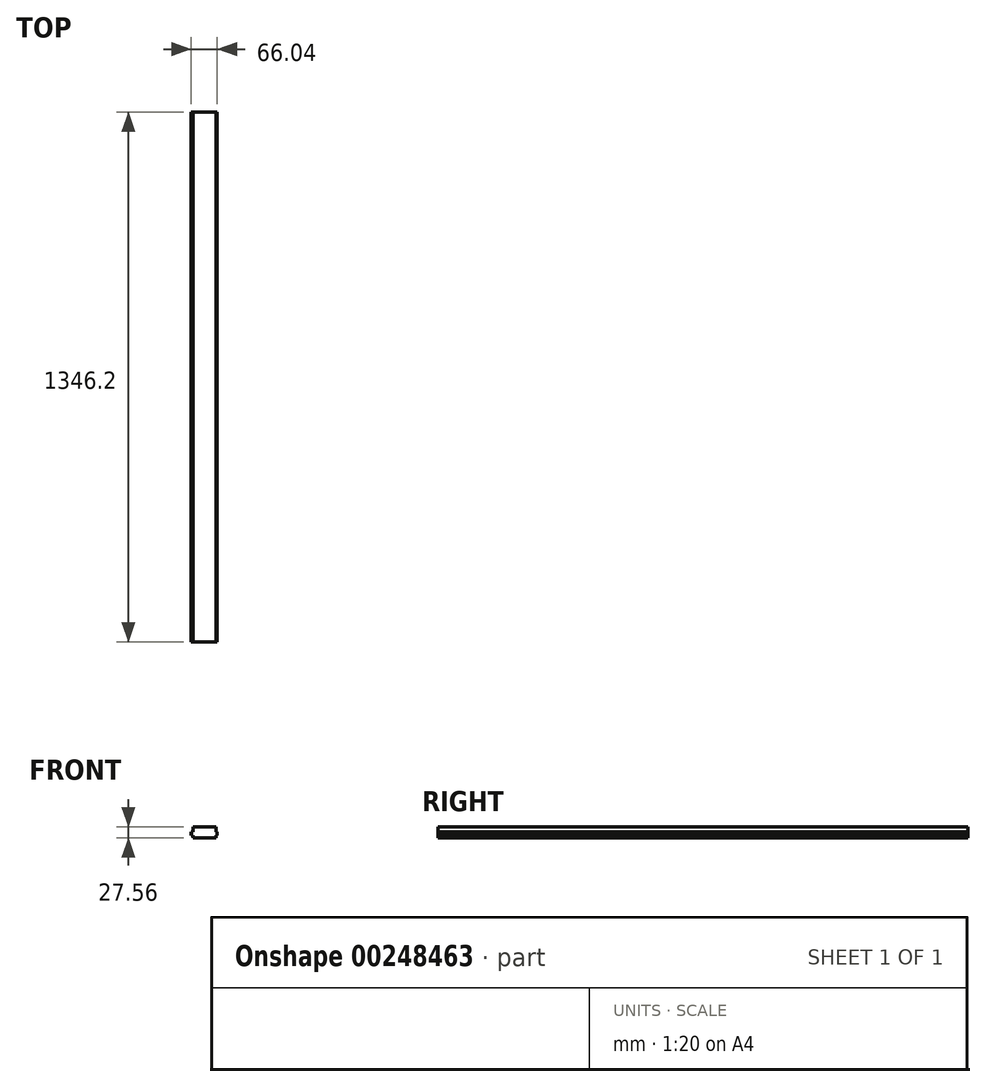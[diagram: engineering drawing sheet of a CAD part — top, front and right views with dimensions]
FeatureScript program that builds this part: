
annotation { "Feature Type Name" : "Feature", "Feature Type Description" : "" }
export const myFeature = defineFeature(function(context is Context, id is Id, definition is map)
    precondition{}
    {
        {
            var Q0;
            Q0=qCreatedBy(makeId("Front.planeOp"),FACE);
            var sketch = newSketch(context, id + "F0", { "sketchPlane" : qUnion([Q0])});
            skLineSegment(sketch, "E0", {"start": v(0, 0) * mm, "end": v(0, 73.02) * mm, "construction": true});
            skLineSegment(sketch, "E1", {"start": v(0, 0) * mm, "end": v(-29.21, 0) * mm});
            skLineSegment(sketch, "E2", {"start": v(-29.21, 0) * mm, "end": v(-29.21, 5.97) * mm});
            skLineSegment(sketch, "E3", {"start": v(-29.21, 5.97) * mm, "end": v(-33.02, 5.97) * mm});
            skLineSegment(sketch, "E4", {"start": v(-33.02, 5.97) * mm, "end": v(-33.02, 14.86) * mm});
            skLineSegment(sketch, "E5", {"start": v(-33.02, 14.86) * mm, "end": v(-29.21, 14.86) * mm});
            skLineSegment(sketch, "E6", {"start": v(-29.21, 14.86) * mm, "end": v(-29.21, 27.56) * mm});
            skLineSegment(sketch, "E7", {"start": v(-29.21, 27.56) * mm, "end": v(0, 27.56) * mm});
            skLineSegment(sketch, "E8.MirrorCS", {"start": v(29.21, 27.56) * mm, "end": v(0, 27.56) * mm});
            skLineSegment(sketch, "E9.MirrorCS", {"start": v(0, 0) * mm, "end": v(29.21, 0) * mm});
            skLineSegment(sketch, "E10.MirrorCS", {"start": v(29.21, 0) * mm, "end": v(29.21, 5.97) * mm});
            skLineSegment(sketch, "E11.MirrorCS", {"start": v(29.21, 5.97) * mm, "end": v(33.02, 5.97) * mm});
            skLineSegment(sketch, "E12.MirrorCS", {"start": v(33.02, 5.97) * mm, "end": v(33.02, 14.86) * mm});
            skLineSegment(sketch, "E13.MirrorCS", {"start": v(33.02, 14.86) * mm, "end": v(29.21, 14.86) * mm});
            skLineSegment(sketch, "E14.MirrorCS", {"start": v(29.21, 14.86) * mm, "end": v(29.21, 27.56) * mm});
            skSolve(sketch);
        }
        {
            var Q0;
            Q0 = qSketchRegion(id + "F0", true);
            extrude(context, id + "F1", {"entities" : qUnion([Q0]), "endBound" : BoundingType.SYMMETRIC, "oppositeDirection" : true, "depth" : 1346.2 * mm});
        }
    });
